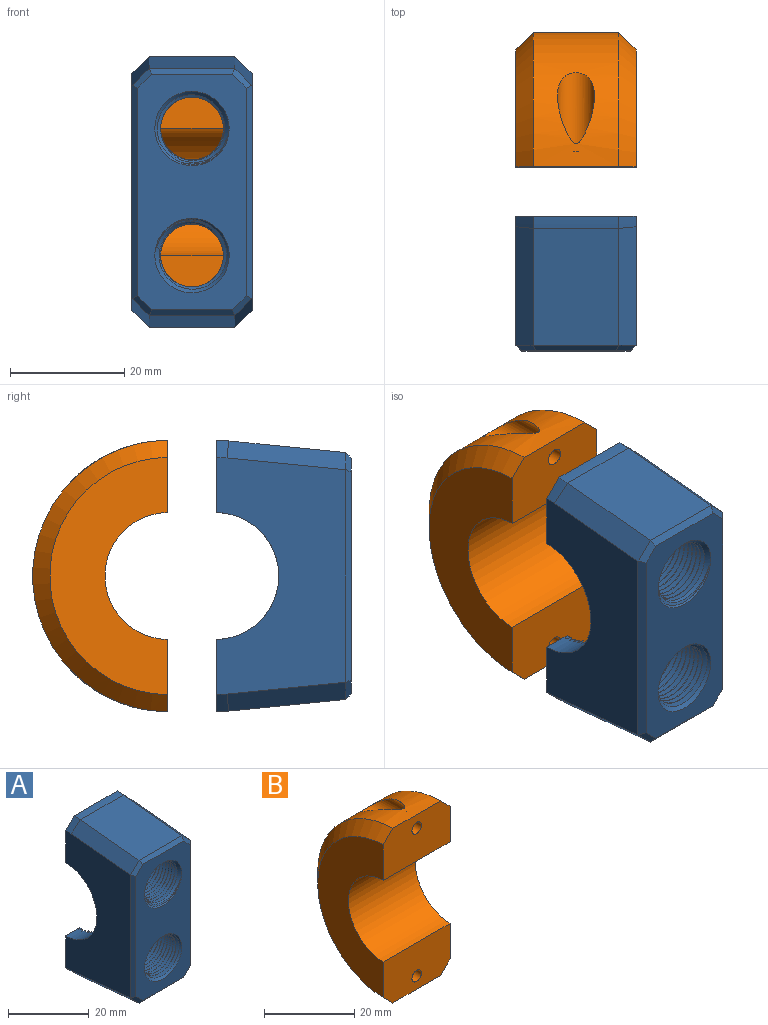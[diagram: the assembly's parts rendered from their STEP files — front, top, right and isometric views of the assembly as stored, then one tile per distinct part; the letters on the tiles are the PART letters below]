
ASSEMBLY  parts=2 mates=2
PART A: 116 faces, bbox 21x24x47.5 mm
  f0: cylinder r=5.5mm len=11mm, axis (0,-1,0), area 1.8mm2, adj f26,f27,f100,f101,f102
  f1: cylinder r=5.5mm len=11mm, axis (0,-1,0), area 1.8mm2, adj f26,f27,f103,f104
  f2: cylinder r=5.5mm len=11mm, axis (0,-1,0), area 1.8mm2, adj f26,f27,f105,f106
  f3: cylinder r=5.5mm len=11mm, axis (0,-1,0), area 1.9mm2, adj f26,f27,f107,f108
  f4: cylinder r=5.5mm len=11mm, axis (0,-1,0), area 2mm2, adj f26,f27,f109,f110
  f5: cylinder r=5.5mm len=11mm, axis (0,-1,0), area 2.1mm2, adj f26,f27,f111,f112
  f6: cylinder r=5.5mm len=11mm, axis (0,-1,0), area 2.3mm2, adj f26,f27,f113,f115
  f7: cylinder r=5.5mm len=11mm, axis (0,-1,0), area 2.6mm2, adj f26,f27,f98,f114
  f8: cylinder r=5.5mm len=11mm, axis (0,-1,0), area 2.9mm2, adj f26,f51,f95,f97
  f9: cylinder r=5.5mm len=11mm, axis (0,-1,0), area 2.9mm2, adj f50,f51,f93,f96
  f10: cylinder r=5.5mm len=11mm, axis (0,-1,0), area 2.9mm2, adj f50,f51,f92,f94
  f11: cylinder r=5.5mm len=11mm, axis (0,-1,0), area 13.8mm2, adj f50,f60,f90,f91
  f12: cylinder r=5.5mm len=11mm, axis (0,-1,0), area 4.3mm2, adj f27,f34,f99
  f13: cylinder r=5.5mm len=11mm, axis (0,-1,0), area 1.8mm2, adj f26,f27,f85,f87,f89
  f14: cylinder r=5.5mm len=11mm, axis (0,-1,0), area 1.8mm2, adj f26,f27,f83,f86
  f15: cylinder r=5.5mm len=11mm, axis (0,-1,0), area 1.8mm2, adj f26,f27,f81,f84
  f16: cylinder r=5.5mm len=11mm, axis (0,-1,0), area 1.9mm2, adj f26,f27,f79,f82
  f17: cylinder r=5.5mm len=11mm, axis (0,-1,0), area 2mm2, adj f26,f27,f77,f80
  f18: cylinder r=5.5mm len=11mm, axis (0,-1,0), area 2.1mm2, adj f26,f27,f75,f78
  f19: cylinder r=5.5mm len=11mm, axis (0,-1,0), area 2.3mm2, adj f26,f27,f73,f76
  f20: cylinder r=5.5mm len=11mm, axis (0,-1,0), area 2.6mm2, adj f26,f27,f72,f74
  f21: cylinder r=5.5mm len=11mm, axis (0,-1,0), area 2.9mm2, adj f27,f50,f70,f71
  f22: cylinder r=5.5mm len=11mm, axis (0,-1,0), area 2.9mm2, adj f50,f51,f67,f69
  f23: cylinder r=5.5mm len=11mm, axis (0,-1,0), area 2.9mm2, adj f50,f51,f66,f68
  f24: cylinder r=5.5mm len=11mm, axis (0,-1,0), area 13.8mm2, adj f51,f63,f64,f65
  f25: cylinder r=5.5mm len=11mm, axis (0,-1,0), area 4.3mm2, adj f26,f28,f88
  f26: cylinder r=11.11mm len=22.22mm, axis (-1,0,0), area 214.2mm2, adj f0,f1,f2,f3,f4,f5,f6,f7
  f27: cylinder r=11.11mm len=22.22mm, axis (-1,0,0), area 214.2mm2, adj f0,f1,f2,f3,f4,f5,f6,f7
  f28: plane 21x12.64mm, normal (0,1,0), area 199.8mm2, adj f25,f26,f27,f29,f35,f36,f42,f44
  f29: cylinder r=23.75mm len=15mm, axis (-1,0,0), area 32.4mm2, adj f28,f30,f42,f44
  f30: plane 20.49x15mm, normal (0,-0.1,1), area 308.9mm2, adj f29,f41,f43,f52,f54,f56
  f31: plane 41.19x19mm, normal (0,-1,0), area 505.4mm2, adj f52,f53,f54,f55,f56,f57,f58,f59
  f32: plane 20.49x15mm, normal (0,-0.1,-1), area 308.9mm2, adj f33,f37,f39,f55,f57,f59
  f33: cylinder r=23.75mm len=15mm, axis (-1,0,0), area 32.4mm2, adj f32,f34,f38,f40
  f34: plane 21x12.64mm, normal (0,1,0), area 199.8mm2, adj f12,f26,f27,f33,f35,f36,f38,f40
  f35: plane 41.5x22.55mm, normal (1,0,0), area 699.2mm2, adj f27,f28,f34,f39,f40,f43,f44,f58
  f36: plane 41.5x22.55mm, normal (-1,0,0), area 699.2mm2, adj f26,f28,f34,f37,f38,f41,f42,f53
  f37: plane 20.76x5.05mm, normal (-0.71,-0.07,-0.7), area 87.9mm2, adj f32,f36,f38,f53,f55
  f38: cone r=23.75mm half-angle=45deg, axis (1,0,0), area 8.5mm2, adj f33,f34,f36,f37
  f39: plane 20.76x5.05mm, normal (0.71,-0.07,-0.7), area 87.9mm2, adj f32,f35,f40,f58,f59
  f40: cone r=20.75mm half-angle=45deg, axis (-1,0,0), area 8.5mm2, adj f33,f34,f35,f39
  f41: plane 20.76x5.05mm, normal (-0.71,-0.07,0.7), area 87.9mm2, adj f30,f36,f42,f52,f53
  f42: cone r=23.75mm half-angle=45deg, axis (1,0,0), area 8.5mm2, adj f28,f29,f36,f41
  f43: plane 20.76x5.05mm, normal (0.71,-0.07,0.7), area 87.9mm2, adj f30,f35,f44,f56,f58
  f44: cone r=20.75mm half-angle=45deg, axis (-1,0,0), area 8.5mm2, adj f28,f29,f35,f43
  f45: cylinder r=1.7mm len=5mm, axis (0,1,0), area 53.4mm2, adj f28,f46
  f46: cone r=0mm half-angle=59deg, axis (0,1,0), area 10.6mm2, adj f45
  f47: cylinder r=1.7mm len=5mm, axis (0,1,0), area 53.4mm2, adj f34,f48
  f48: cone r=0mm half-angle=59deg, axis (0,1,0), area 10.6mm2, adj f47
  f49: cylinder r=13.84mm len=11.54mm, axis (1,0,0), area 56.5mm2, adj f50,f51,f65,f91
  f50: plane 12.46x4.33mm, normal (1,0,0), area 32.7mm2, adj f9,f10,f11,f21,f22,f23,f26,f49
  f51: plane 12.46x4.33mm, normal (-1,0,0), area 32.7mm2, adj f8,f9,f10,f22,f23,f24,f27,f49
  f52: plane 3.42x3.34mm, normal (-0.48,-0.73,0.48), area 5.2mm2, adj f30,f31,f41,f53,f54
  f53: plane 37.3x1mm, normal (-0.71,-0.71,0), area 52.1mm2, adj f31,f36,f37,f41,f52,f55
  f54: plane 14.92x1mm, normal (0,-0.74,0.67), area 19.5mm2, adj f30,f31,f52,f56
  f55: plane 3.42x3.34mm, normal (-0.48,-0.73,-0.48), area 5.2mm2, adj f31,f32,f37,f53,f57
  f56: plane 3.42x3.34mm, normal (0.48,-0.73,0.48), area 5.2mm2, adj f30,f31,f43,f54,f58
  f57: plane 14.92x1mm, normal (0,-0.74,-0.67), area 19.5mm2, adj f31,f32,f55,f59
  f58: plane 37.3x1mm, normal (0.71,-0.71,0), area 52.1mm2, adj f31,f35,f39,f43,f56,f59
  f59: plane 3.42x3.34mm, normal (0.48,-0.73,-0.48), area 5.2mm2, adj f31,f32,f39,f57,f58
  f60: cone r=5.5mm half-angle=45deg, axis (0,-1,0), area 7.6mm2, adj f11,f61,f90,f91
  f61: cone r=5.5mm half-angle=45deg, axis (0,-1,0), area 25.7mm2, adj f31,f60,f91
  f62: cone r=5.5mm half-angle=45deg, axis (0,-1,0), area 32.8mm2, adj f31,f63,f64,f65
  f63: cone r=5.5mm half-angle=45deg, axis (0,-1,0), area 0.5mm2, adj f24,f62,f64
  f64: bspline ~14.7x12.73mm, area 399mm2, adj f24,f51,f62,f63,f65
  f65: bspline ~14.7x12.78mm, area 414.8mm2, adj f24,f49,f50,f51,f62,f64,f66
  f66: bspline ~14.7x12.73mm, area 31.3mm2, adj f23,f50,f51,f65
  f67: bspline ~14.7x12.73mm, area 31.3mm2, adj f22,f50,f51,f68
  f68: bspline ~14.7x12.73mm, area 31.3mm2, adj f23,f50,f51,f67
  f69: bspline ~14.7x12.73mm, area 31.2mm2, adj f22,f27,f50,f51,f70
  f70: bspline ~14.7x12.73mm, area 30.6mm2, adj f21,f27,f50,f69
  f71: bspline ~14.7x12.73mm, area 29.2mm2, adj f21,f26,f27,f50,f72
  f72: bspline ~12.86x12.73mm, area 27.5mm2, adj f20,f26,f27,f71
  f73: bspline ~12.86x12.73mm, area 24.6mm2, adj f19,f26,f27,f74
  f74: bspline ~12.86x12.73mm, area 25.8mm2, adj f20,f26,f27,f73
  f75: bspline ~12.86x12.73mm, area 22.7mm2, adj f18,f26,f27,f76
  f76: bspline ~12.86x12.73mm, area 23.5mm2, adj f19,f26,f27,f75
  f77: bspline ~12.86x12.73mm, area 21.3mm2, adj f17,f26,f27,f78
  f78: bspline ~12.86x12.73mm, area 21.9mm2, adj f18,f26,f27,f77
  f79: bspline ~12.86x12.73mm, area 20.2mm2, adj f16,f26,f27,f80
  f80: bspline ~12.86x12.73mm, area 20.7mm2, adj f17,f26,f27,f79
  f81: bspline ~12.86x12.73mm, area 19.4mm2, adj f15,f26,f27,f82
  f82: bspline ~12.86x12.73mm, area 19.8mm2, adj f16,f26,f27,f81
  f83: bspline ~12.86x12.73mm, area 18.8mm2, adj f14,f26,f27,f84
  f84: bspline ~12.86x12.73mm, area 19.1mm2, adj f15,f26,f27,f83
  f85: bspline ~12.86x12.73mm, area 18.4mm2, adj f13,f26,f27,f86
  f86: bspline ~12.86x12.73mm, area 18.6mm2, adj f14,f26,f27,f85
  f87: bspline ~12.86x12.73mm, area 18.3mm2, adj f13,f26,f88,f89
  f88: bspline ~12.86x12.73mm, area 18.2mm2, adj f25,f26,f87,f89
  f89: plane 0.9x0.87mm, normal (0,0,1), area 0.4mm2, adj f13,f87,f88
  f90: bspline ~14.7x12.73mm, area 399.1mm2, adj f11,f50,f60,f91
  f91: bspline ~14.7x12.78mm, area 414.8mm2, adj f11,f49,f50,f51,f60,f61,f90,f92
  f92: bspline ~14.7x12.73mm, area 31.3mm2, adj f10,f50,f51,f91
  f93: bspline ~14.7x12.73mm, area 31.3mm2, adj f9,f50,f51,f94
  f94: bspline ~14.7x12.73mm, area 31.3mm2, adj f10,f50,f51,f93
  f95: bspline ~14.7x12.73mm, area 30.6mm2, adj f8,f26,f51,f96
  f96: bspline ~14.7x12.73mm, area 31.2mm2, adj f9,f26,f50,f51,f95
  f97: bspline ~14.7x12.73mm, area 29.2mm2, adj f8,f26,f27,f51,f98
  f98: bspline ~12.86x12.73mm, area 27.5mm2, adj f7,f26,f27,f97
  f99: bspline ~12.86x12.73mm, area 18.2mm2, adj f12,f27,f100,f101
  f100: bspline ~12.86x12.73mm, area 18.3mm2, adj f0,f27,f99,f101
  f101: plane 0.9x0.87mm, normal (0,0,-1), area 0.4mm2, adj f0,f99,f100
  f102: bspline ~12.86x12.73mm, area 18.4mm2, adj f0,f26,f27,f103
  f103: bspline ~12.86x12.73mm, area 18.6mm2, adj f1,f26,f27,f102
  f104: bspline ~12.86x12.73mm, area 18.8mm2, adj f1,f26,f27,f105
  f105: bspline ~12.86x12.73mm, area 19.1mm2, adj f2,f26,f27,f104
  f106: bspline ~12.86x12.73mm, area 19.4mm2, adj f2,f26,f27,f107
  f107: bspline ~12.86x12.73mm, area 19.8mm2, adj f3,f26,f27,f106
  f108: bspline ~12.86x12.73mm, area 20.2mm2, adj f3,f26,f27,f109
  f109: bspline ~12.86x12.73mm, area 20.7mm2, adj f4,f26,f27,f108
  f110: bspline ~12.86x12.73mm, area 21.3mm2, adj f4,f26,f27,f111
  f111: bspline ~12.86x12.73mm, area 21.9mm2, adj f5,f26,f27,f110
  f112: bspline ~12.86x12.73mm, area 22.7mm2, adj f5,f26,f27,f113
  f113: bspline ~12.86x12.73mm, area 23.5mm2, adj f6,f26,f27,f112
  f114: bspline ~12.86x12.73mm, area 25.8mm2, adj f7,f26,f27,f115
  f115: bspline ~12.86x12.73mm, area 24.6mm2, adj f6,f26,f27,f114
PART B: 14 faces, bbox 21x23.6x47.5 mm
  f0: cylinder r=23.75mm len=47.5mm, axis (-1,0,0), area 972.7mm2, adj f1,f3,f6,f7,f8,f11
  f1: plane 21x12.64mm, normal (0,-1,0), area 249.3mm2, adj f0,f2,f4,f5,f6,f7,f9
  f2: cylinder r=11.11mm len=22.22mm, axis (-1,0,0), area 724.7mm2, adj f1,f3,f4,f5
  f3: plane 21x12.64mm, normal (0,-1,0), area 249.3mm2, adj f0,f2,f4,f5,f6,f7,f12
  f4: plane 41.5x20.55mm, normal (1,0,0), area 478.5mm2, adj f1,f2,f3,f7
  f5: plane 41.5x20.55mm, normal (-1,0,0), area 478.5mm2, adj f1,f2,f3,f6
  f6: cone r=23.75mm half-angle=45deg, axis (1,0,0), area 294.9mm2, adj f0,f1,f3,f5
  f7: cone r=20.75mm half-angle=45deg, axis (-1,0,0), area 294.9mm2, adj f0,f1,f3,f4
  f8: cylinder r=3.25mm len=13.83mm, axis (0,1,0), area 179.4mm2, adj f0,f10
  f9: cylinder r=1.5mm len=3mm, axis (0,1,0), area 25.4mm2, adj f1,f10
  f10: plane 6.5x6.5mm, normal (0,1,0), area 26.1mm2, adj f8,f9
  f11: cylinder r=3.25mm len=13.83mm, axis (0,1,0), area 179.2mm2, adj f0,f13
  f12: cylinder r=1.5mm len=3mm, axis (0,1,0), area 25.4mm2, adj f3,f13
  f13: plane 6.5x6.5mm, normal (0,1,0), area 26.1mm2, adj f11,f12
PLACE A t=(-13.8,-1.86,0.51)mm
PLACE B t=(-13.8,6.34,0.51)mm
MATE planar B.f5 <-> A.f36  axis (-1,0,0) through (-13.8,16.88,0.51)mm
MATE parallel B.f3 <-> A.f34  axis (0,-1,0) through (7.2,6.54,-20.24)mm
